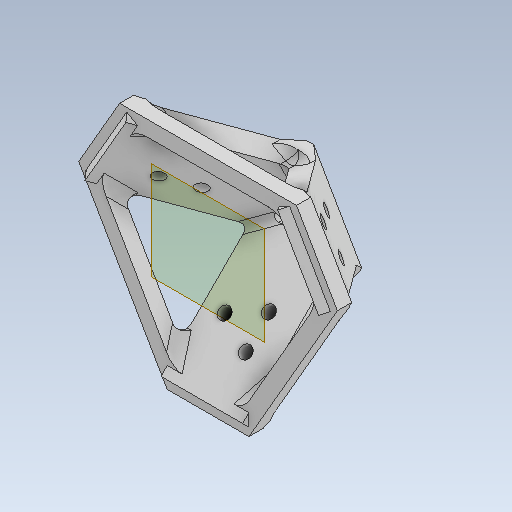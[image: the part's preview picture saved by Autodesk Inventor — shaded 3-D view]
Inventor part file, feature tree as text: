
AUTODESK INVENTOR PART (.ipt)
format: ipt  version: 2020 (Build 240168000, 168)  size: 496,128 bytes
history: native  units: mm
features: extrude x15, sketch x15, projected_geometry x11, reference x10, fillet x7, other x6, thicken_offset x3, pattern_circular x1, chamfer x1, plane x1
ambient origin geometry x8: Origin, YZ Plane, XZ Plane, XY Plane, X Axis, Y Axis, Z Axis, Center Point
bodies: Solid1 (feature_tree)
feature tree (70):
  extrude  "Extrusion1"  Depth=20.0mm
  extrude  "Extrusion2"  Depth=5.0mm
  extrude  "Extrusion3"  Depth=20.0mm
  extrude  "Extrusion4"  Depth=5.0mm
  extrude  "Extrusion5"  Depth=5.0mm
  extrude  "Extrusion6"  Depth=20.0mm
  extrude  "Extrusion7"  Depth=20.0mm TaperAngle=0.0deg
  pattern_circular  "Circular Pattern1"  Count=2  [1 undecoded]
  extrude  "Extrusion8"  Depth=35.0mm
  fillet  "Fillet1"  Radius=20.0mm
  fillet  "Fillet2"  Radius=20.0mm
  fillet  "Fillet3"  Radius=20.0mm
  chamfer  "Chamfer1"  Distance=5.0mm
  extrude  "Extrusion9"  Depth=5.0mm TaperAngle=0.0deg
  extrude  "Extrusion10"  Depth=1.0mm
  extrude  "Extrusion11"  Depth=3.0mm TaperAngle=45.0deg
  extrude  "Extrusion12"  Depth=5.0mm TaperAngle=0.0deg
  extrude  "Extrusion13"  Depth=3.0mm
  extrude  "Extrusion14"  Depth=1.0mm
  plane  "Work Plane1"
  extrude  "Extrusion15"  Depth=1.0mm TaperAngle=0.0deg
  thicken_offset  "Thicken1"
  thicken_offset  "Thicken2"
  thicken_offset  "Thicken3"
  fillet  "Fillet4"  Radius=3.0mm
  fillet  "Fillet5"  Radius=3.0mm
  fillet  "Fillet6"  Radius=3.0mm
  fillet  "Fillet7"  Radius=5.0mm
  sketch  "Sketch1"  dims[d0=20.0mm d1=20.0mm]
  sketch  "Sketch2"  dims[d2=60.0deg d3=5.0mm]
  projected_geometry  "Projected Loop1"
  sketch  "Sketch3"  dims[d4=20.0mm d5=20.0mm]
  projected_geometry  "Projected Loop2"
  sketch  "Sketch4"  dims[d6=5.0mm d7=5.0mm]
  projected_geometry  "Projected Loop3"
  sketch  "Sketch5"  dims[d8=20.0mm d9=5.0mm]
  projected_geometry  "Projected Loop4"
  sketch  "Sketch6"  dims[d10=3.0mm d11=0.0mm d12=20.0mm]
  projected_geometry  "Projected Loop5"
  sketch  "Sketch7"  dims[d13=20.0mm d14=20.0mm d15=0.0mm d16=20.0mm d17=0.0mm]
  sketch  "Sketch8"  dims[d18=5.0mm d19=35.0mm d20=20.0mm d21=0.0mm d22=20.0mm d23=0.0mm d24=20.0mm d25=0.0mm]
  sketch  "Sketch9"  dims[d26=3.0mm d27=5.0mm d28=0.0mm]
  projected_geometry  "Projected Loop6"
  sketch  "Sketch10"  dims[d29=30.0mm d30=360.0deg d32=5.0mm d33=0.0mm]
  projected_geometry  "Projected Loop7"
  sketch  "Sketch11"  dims[d34=1.0mm d35=2.0mm]
  projected_geometry  "Projected Loop8"
  sketch  "Sketch12"  dims[d36=2.0mm d37=3.0mm d38=2.0mm d39=45.0deg]
  reference  "Reference1"
  reference  "Reference2"
  reference  "Reference3"
  reference  "Reference4"
  sketch  "Sketch13"  dims[d40=5.0mm d41=0.0mm d42=5.0mm d43=0.0mm]
  reference  "Reference5"
  reference  "Reference6"
  reference  "Reference7"
  sketch  "Sketch14"  dims[d44=5.0mm d45=0.0mm d46=3.0mm]
  reference  "Reference8"
  reference  "Reference9"
  reference  "Reference10"
  sketch  "Sketch15"  dims[d47=3.0mm d48=3.0mm d49=5.0mm d50=0.0mm d51=3.0mm d52=3.0mm d53=3.0mm d54=5.0mm d55=0.0mm d56=3.0mm d57=3.0mm d58=3.0mm d59=5.0mm d60=0.0mm d61=-25.0mm d62=3.5mm d63=0.0mm d64=2.0mm d65=2.0mm d66=2.0mm d67=2.0mm d68=2.0mm d69=2.0mm d70=3.0mm d71=3.0mm d72=4.0mm d73=1.0mm]
  projected_geometry  "Projected Loop9"
  projected_geometry  "Projected Loop10"
  projected_geometry  "Projected Loop11"
  parser-record x1  (decoder bookkeeping rows leaked as tree rows — omitted from the tree; the rows remain in map.json)
  other  "delta_1.iam"
  other  "arm_shift_1:3"
  other  "motor_holder_1:1"
  other  "arm_shift_1:2"
  other  "arm_shift_1:1"
note: 1 required parameter value undecoded (feature->parameter linkage not recoverable at this tier; creation-order binding heuristic only, values carry confidence <= 0.55)
note: 1 file-system path scrubbed to <path> (originals preserved in map.json)
